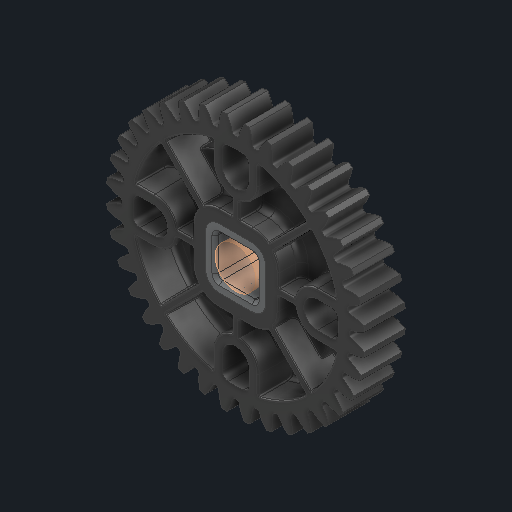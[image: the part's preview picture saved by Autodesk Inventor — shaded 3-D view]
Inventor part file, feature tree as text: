
AUTODESK INVENTOR PART (.ipt)
format: ipt  version: 2025 (Build 290162000, 162)  size: 2,115,072 bytes
history: native  units: in
note: dims shown in document units (in); Inventor stores cm internally (conversion verified against a paired STEP export)
features: other x6, sketch x2
ambient origin geometry x8: Origin, YZ Plane, XZ Plane, XY Plane, X Axis, Y Axis, Z Axis, Center Point
bodies: Solid1 (feature_tree), Solid2 (feature_tree)
feature tree (8):
  other  "Half Cut HS 36T Gear, No Insert.ipt"
  other  "Solid1::Half Cut HS 36T Gear, No Insert.ipt"
  other  "Solid2::Half Cut HS 36T Gear, No Insert.ipt"
  other  "TaggingFeature1"
  sketch  "Sketch1"  dims[d0=0.3937in]
  sketch  "Sketch2"
  other  "Srf1"
  other  "Srf1::Derived"
